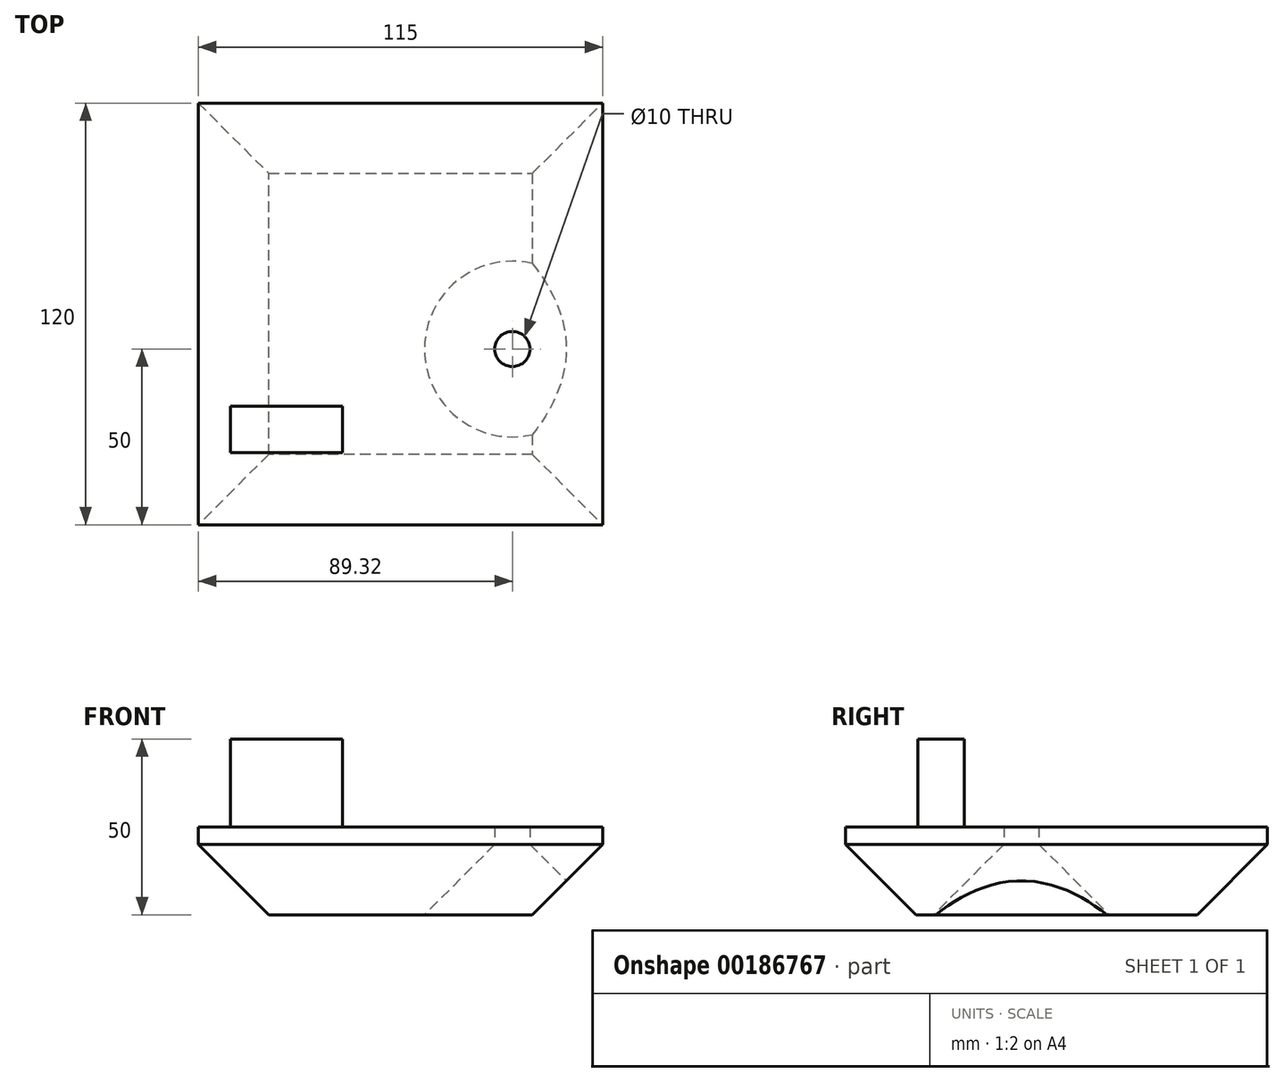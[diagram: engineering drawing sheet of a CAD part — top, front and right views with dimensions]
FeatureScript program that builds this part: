
annotation { "Feature Type Name" : "Feature", "Feature Type Description" : "" }
export const myFeature = defineFeature(function(context is Context, id is Id, definition is map)
    precondition{}
    {
        {
            var Q0;
            Q0=qCreatedBy(makeId("Top.planeOp"),FACE);
            var sketch = newSketch(context, id + "F0", { "sketchPlane" : qUnion([Q0])});
            skCircle(sketch, "E0", {"center": v(-35, 0) * mm, "radius": 5 * mm});
            skLineSegment(sketch, "E1.bottom", {"start": v(-124.32, 70) * mm, "end": v(-9.32, 70) * mm});
            skLineSegment(sketch, "E1.top", {"start": v(-124.32, -50) * mm, "end": v(-9.32, -50) * mm});
            skLineSegment(sketch, "E1.left", {"start": v(-124.32, 70) * mm, "end": v(-124.32, -50) * mm});
            skLineSegment(sketch, "E1.right", {"start": v(-9.32, 70) * mm, "end": v(-9.32, -50) * mm});
            skSolve(sketch);
        }
        {
            var Q0;
            Q0 = qSketchRegion(id + "F0", true);
            extrude(context, id + "F1", {"entities" : qUnion([Q0]), "depth" : 25 * mm});
        }
        {
            var Q0;
            Q0=makeQuery(id+"F1.opExtrude","CAP_FACE",FACE,{"disambiguationData":[OSD([sQuery(id+"F0.wireOp",EDGE,"E0"),sQuery(id+"F0.wireOp",EDGE,"E1.bottom"),sQuery(id+"F0.wireOp",EDGE,"E1.top"),sQuery(id+"F0.wireOp",EDGE,"E1.left"),sQuery(id+"F0.wireOp",EDGE,"E1.right")])],"isStart":false});
            var sketch = newSketch(context, id + "F2", { "sketchPlane" : qUnion([Q0])});
            skLineSegment(sketch, "E2.bottom", {"start": v(-115.2, -16.27) * mm, "end": v(-83.3, -16.27) * mm});
            skLineSegment(sketch, "E2.top", {"start": v(-115.2, -29.42) * mm, "end": v(-83.3, -29.42) * mm});
            skLineSegment(sketch, "E2.left", {"start": v(-115.2, -16.27) * mm, "end": v(-115.2, -29.42) * mm});
            skLineSegment(sketch, "E2.right", {"start": v(-83.3, -16.27) * mm, "end": v(-83.3, -29.42) * mm});
            skSolve(sketch);
        }
        {
            var Q0;
            Q0 = qSketchRegion(id + "F2", true);
            extrude(context, id + "F3", {"entities" : qUnion([Q0]), "operationType" : NewBodyOperationType.ADD, "depth" : 25 * mm});
        }
        {
            var Q0;
            Q0=makeQuery(id+"F1.opExtrude","CAP_FACE",FACE,{"disambiguationData":[OSD([sQuery(id+"F0.wireOp",EDGE,"E0"),sQuery(id+"F0.wireOp",EDGE,"E1.bottom"),sQuery(id+"F0.wireOp",EDGE,"E1.top"),sQuery(id+"F0.wireOp",EDGE,"E1.left"),sQuery(id+"F0.wireOp",EDGE,"E1.right")])],"isStart":true});
            chamfer(context, id + "F4", {"entities" : qUnion([Q0]), "width" : 20 * mm, "tangentPropagation" : true});
        }
    });
